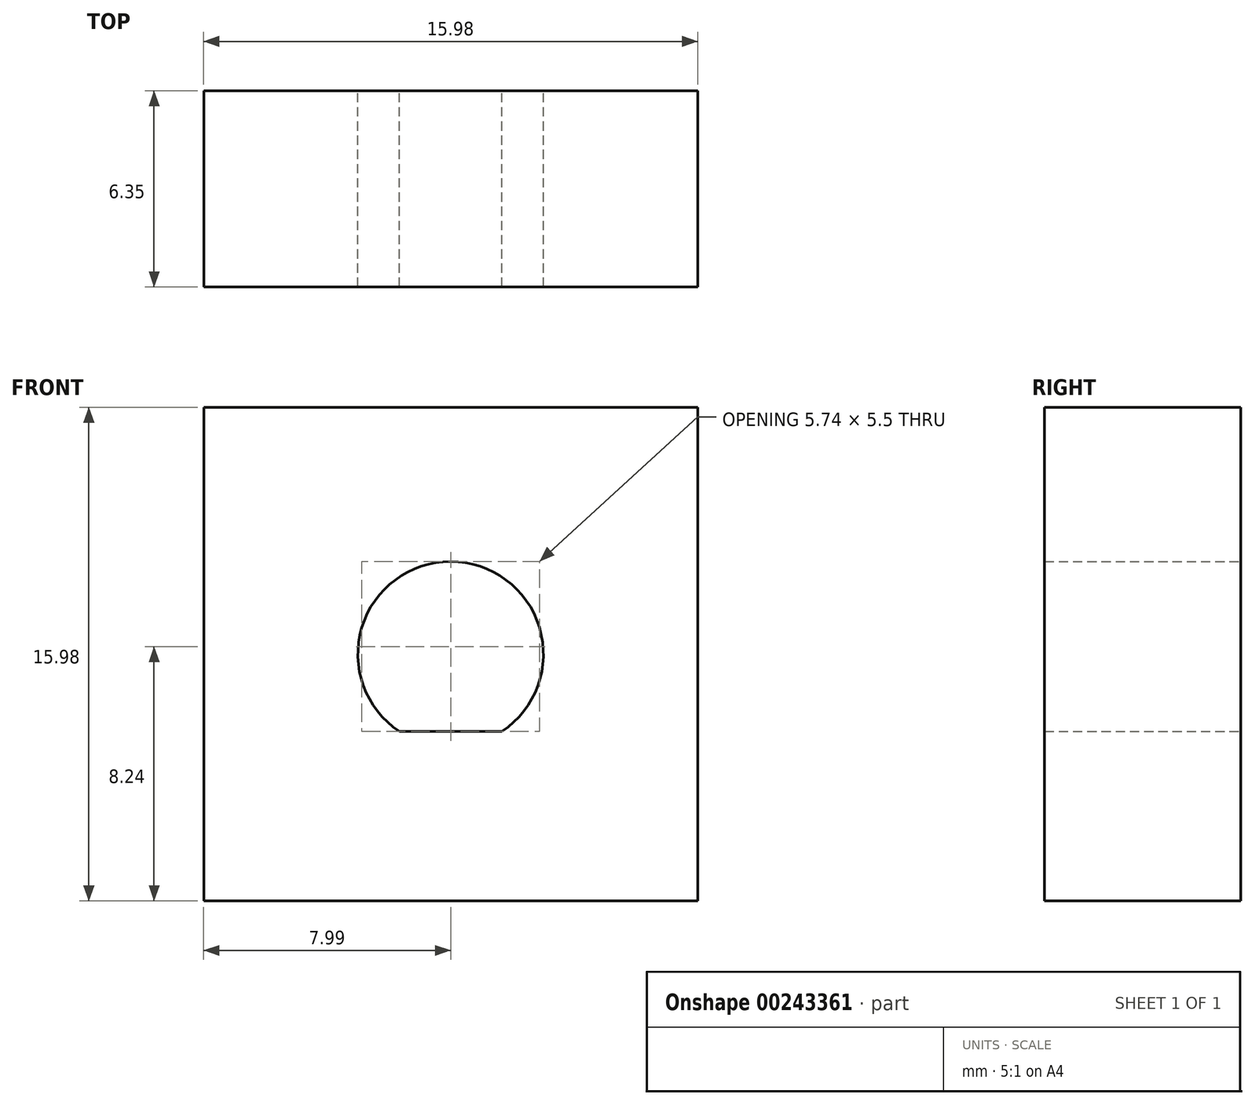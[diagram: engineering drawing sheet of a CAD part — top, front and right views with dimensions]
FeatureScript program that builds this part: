
annotation { "Feature Type Name" : "Feature", "Feature Type Description" : "" }
export const myFeature = defineFeature(function(context is Context, id is Id, definition is map)
    precondition{}
    {
        {
            var Q0;
            Q0=qCreatedBy(makeId("Front.planeOp"),FACE);
            var sketch = newSketch(context, id + "F0", { "sketchPlane" : qUnion([Q0])});
            skLineSegment(sketch, "E0.bottom", {"start": v(-7.99, 7.99) * mm, "end": v(7.99, 7.99) * mm});
            skLineSegment(sketch, "E0.top", {"start": v(-7.99, -7.99) * mm, "end": v(7.99, -7.99) * mm});
            skLineSegment(sketch, "E0.left", {"start": v(-7.99, 7.99) * mm, "end": v(-7.99, -7.99) * mm});
            skLineSegment(sketch, "E0.right", {"start": v(7.99, 7.99) * mm, "end": v(7.99, -7.99) * mm});
            skPoint(sketch, "E0.middle", {"position": v(0, 0) * mm});
            skArc(sketch, "E1", {"start": v(1.66, -2.5) * mm, "mid": v(0, 3) * mm, "end": v(-1.66, -2.5) * mm});
            skLineSegment(sketch, "E2", {"start": v(-1.66, -2.5) * mm, "end": v(1.66, -2.5) * mm});
            skSolve(sketch);
        }
        {
            var Q0;
            Q0 = qSketchRegion(id + "F0", true);
            extrude(context, id + "F1", {"entities" : qUnion([Q0]), "depth" : 6.35 * mm});
        }
    });
